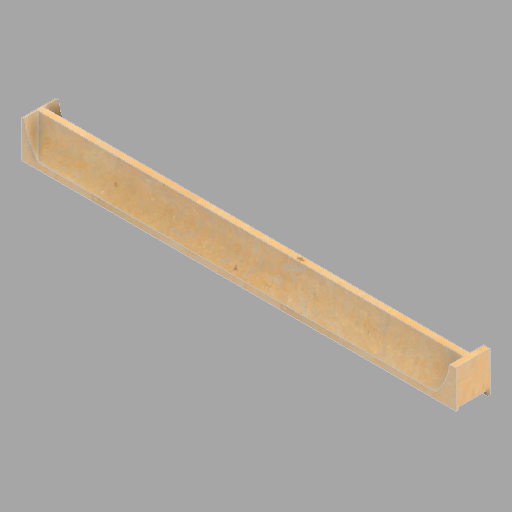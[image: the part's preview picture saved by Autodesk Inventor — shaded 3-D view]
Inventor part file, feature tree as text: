
AUTODESK INVENTOR PART (.ipt)
format: ipt  version: 2022.2 (Build 262287010, 287A)  size: 201,216 bytes
history: native  units: in
note: dims shown in document units (in); Inventor stores cm internally (conversion verified against a paired STEP export)
features: direct_edit x1, revolve x1
ambient origin geometry x8: Origin, YZ Plane, XZ Plane, XY Plane, X Axis, Y Axis, Z Axis, Center Point
bodies: Solid1 (feature_tree), Body1 (feature_tree)
feature tree (2):
  direct_edit  "Direct Edit1"
  revolve  "Rotate1"  Angle=180.0deg
